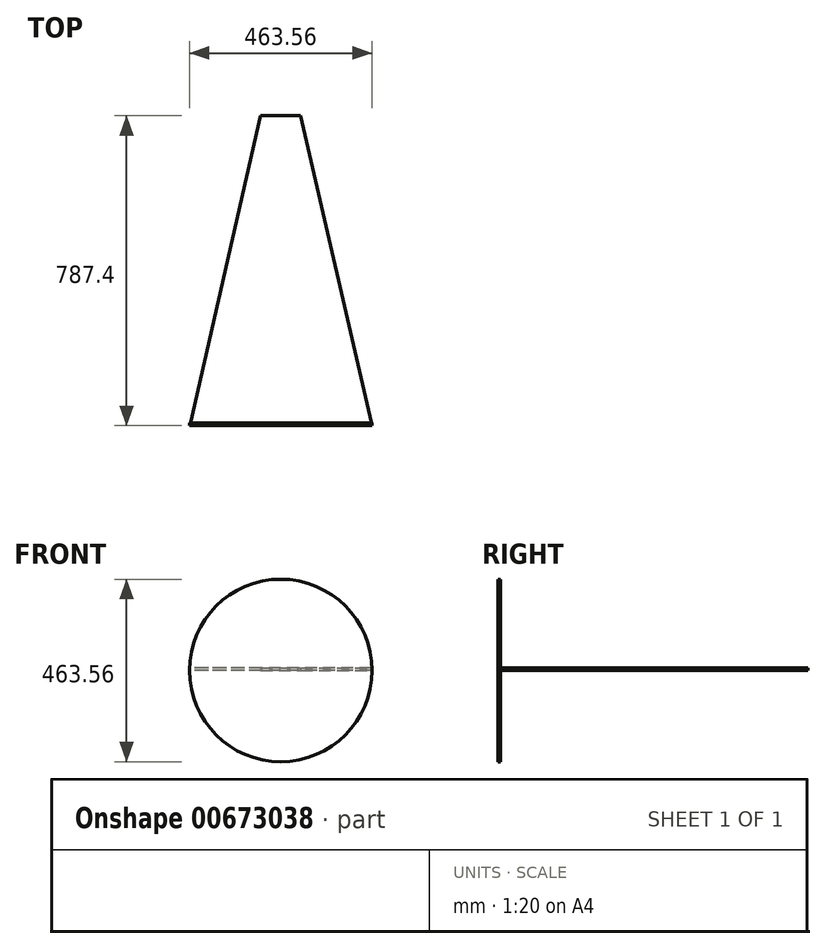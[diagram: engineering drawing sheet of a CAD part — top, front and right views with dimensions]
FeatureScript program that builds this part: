
annotation { "Feature Type Name" : "Feature", "Feature Type Description" : "" }
export const myFeature = defineFeature(function(context is Context, id is Id, definition is map)
    precondition{}
    {
        {
            var Q0;
            Q0=qCreatedBy(makeId("Front.planeOp"),FACE);
            var sketch = newSketch(context, id + "F0", { "sketchPlane" : qUnion([Q0])});
            skCircle(sketch, "E0", {"center": v(0, 0) * mm, "radius": 231.78 * mm});
            skSolve(sketch);
        }
        {
            var Q0;
            Q0 = qSketchRegion(id + "F0", true);
            extrude(context, id + "F1", {"entities" : qUnion([Q0]), "oppositeDirection" : true, "depth" : 6.35 * mm, "offsetDistance" : 25.4 * mm});
        }
        {
            var Q0;
            Q0=qCreatedBy(makeId("Top.planeOp"),FACE);
            var sketch = newSketch(context, id + "F2", { "sketchPlane" : qUnion([Q0])});
            skLineSegment(sketch, "E1", {"start": v(0, 0) * mm, "end": v(0, 787.4) * mm});
            skLineSegment(sketch, "E2", {"start": v(0, 787.4) * mm, "end": v(50.8, 787.4) * mm});
            skLineSegment(sketch, "E3", {"start": v(0, 787.4) * mm, "end": v(-50.8, 787.4) * mm});
            skLineSegment(sketch, "E4", {"start": v(-50.8, 787.4) * mm, "end": v(-230.9, 0) * mm});
            skLineSegment(sketch, "E5", {"start": v(50.8, 787.4) * mm, "end": v(231.38, 0) * mm});
            skLineSegment(sketch, "E6", {"start": v(-230.9, 0) * mm, "end": v(231.38, 0) * mm});
            skSolve(sketch);
        }
        {
            var Q0;
            Q0 = qSketchRegion(id + "F2", true);
            extrude(context, id + "F3", {"entities" : qUnion([Q0]), "operationType" : NewBodyOperationType.ADD, "depth" : 6.35 * mm, "offsetDistance" : 25.4 * mm});
        }
    });
